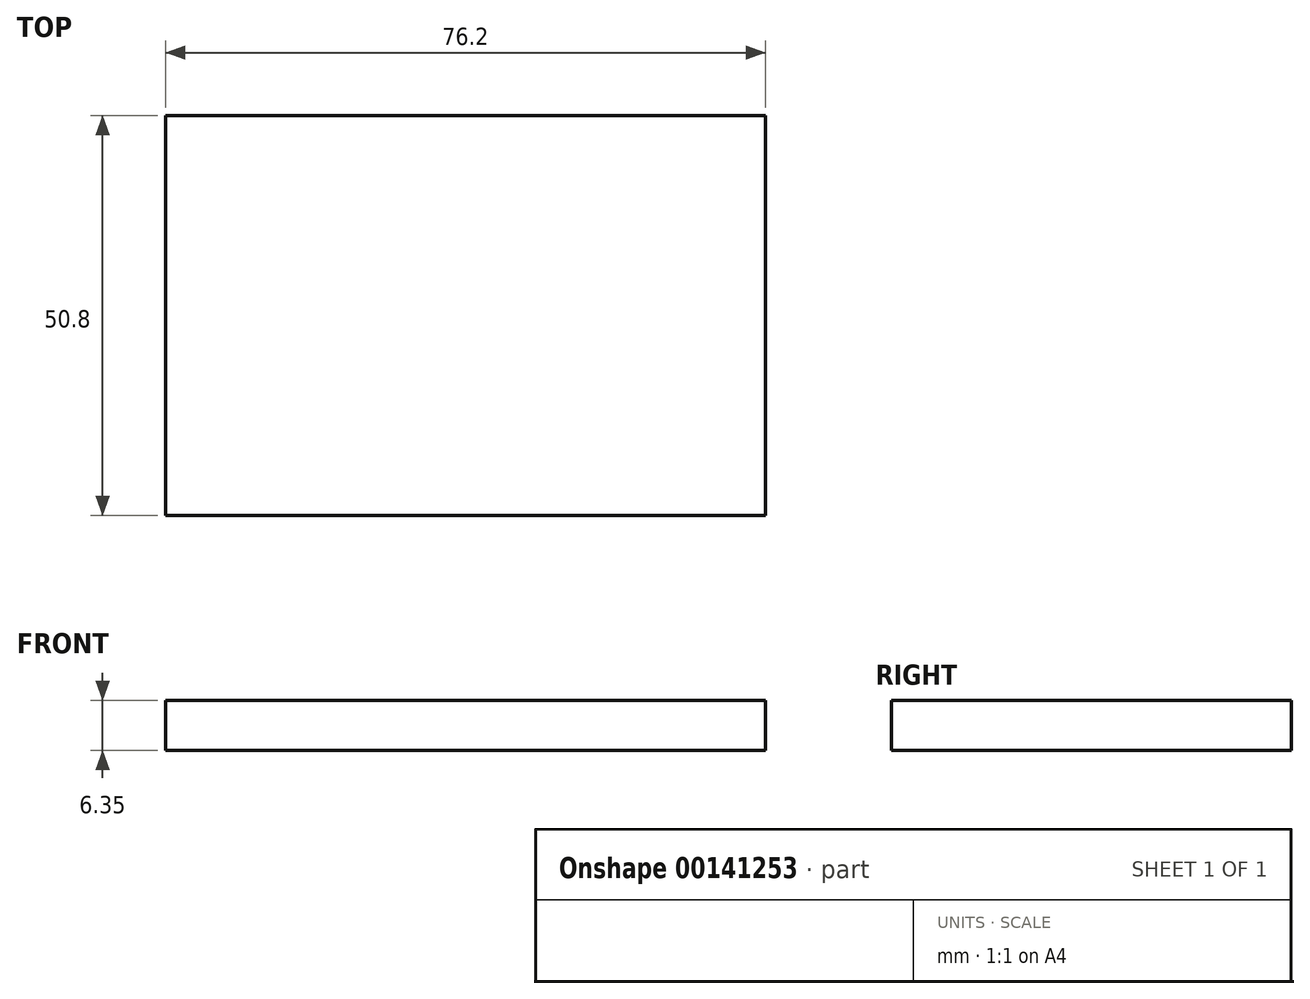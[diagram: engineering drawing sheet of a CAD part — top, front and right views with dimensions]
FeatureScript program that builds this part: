
annotation { "Feature Type Name" : "Feature", "Feature Type Description" : "" }
export const myFeature = defineFeature(function(context is Context, id is Id, definition is map)
    precondition{}
    {
        {
            var Q0;
            Q0=qCreatedBy(makeId("Top.planeOp"),FACE);
            var sketch = newSketch(context, id + "F0", { "sketchPlane" : qUnion([Q0])});
            skLineSegment(sketch, "E0.bottom", {"start": v(0, 0) * mm, "end": v(76.2, 0) * mm});
            skLineSegment(sketch, "E0.top", {"start": v(0, 50.8) * mm, "end": v(76.2, 50.8) * mm});
            skLineSegment(sketch, "E0.left", {"start": v(0, 0) * mm, "end": v(0, 50.8) * mm});
            skLineSegment(sketch, "E0.right", {"start": v(76.2, 0) * mm, "end": v(76.2, 50.8) * mm});
            skSolve(sketch);
        }
        {
            var Q0;
            Q0=makeQuery(id+"F0.imprint","IMPRINT",FACE,{"disambiguationData":[TD([[makeQuery(id+"F0.imprint","IMPRINT",EDGE,{"derivedFrom":sQuery(id+"F0.wireOp",EDGE,"E0.bottom")}),1.0]])]});
            extrude(context, id + "F1", {"entities" : qUnion([Q0]), "oppositeDirection" : true, "depth" : 6.35 * mm});
        }
    });
